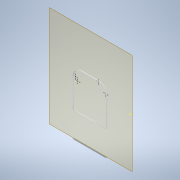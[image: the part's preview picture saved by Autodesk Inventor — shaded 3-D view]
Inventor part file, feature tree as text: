
AUTODESK INVENTOR PART (.ipt)
format: ipt  version: 2021 (Build 250183000, 183)  size: 128,512 bytes
history: native  units: in
note: dims shown in document units (in); Inventor stores cm internally (conversion verified against a paired STEP export)
features: plane x1, extrude x1, sketch x1
ambient origin geometry x8: Origin, YZ Plane, XZ Plane, XY Plane, X Axis, Y Axis, Z Axis, Center Point
bodies: Body1 (feature_tree), Body2 (feature_tree)
feature tree (3):
  plane  "Work Plane1"
  extrude  "Extrusion2"  Depth=1.0in
  sketch  "Sketch2"  dims[d0=135.0deg d1=1.0in d2=0.0625in d5=1.0in d6=0.0in]
